# Revit family: Sanitary_Showers_hansgrohe_24581XXX-Raindance-Alive-Q-Showerpipe-210-340-1jet-EcoSmart-with-ShowerSelect-Comfort_NEW
name_source: partatom
category: Plumbing Fixtures
units: mm (PartAtom-declared; Revit-internal decimal feet)

## family parameters
Always vertical = No
Cut with Voids When Loaded = No
Maintain Annotation Orientation = No
OmniClass Number = 23.31.17.00
OmniClass Title = Showers
Part Type = Normal
Room Calculation Point = No
Round Connector Dimension = Use Diameter
Shared = No
Work Plane-Based = Yes

## types (1)
- Default - please load Revit Family Type Catalog
    Connector Description = Water Inlet 12.7mm
    Default Elevation = 1219 mm
    Description = Raindance Alive Q Showerpipe 210/340 1jet EcoSmart with ShowerSelect Comfort
    Diameter = 13 mm
    Manufacturer = Hansgrohe
    Material 1 = Hansgrohe - Metal - 000 Chrome
    Material 2 = Hansgrohe - Plastic - Graphite
    Model = 24581XXX
    Product Page URL = https://www.hansgrohe.com
    Product data url = https://bimobject.com
    URL = https://www.hansgrohe.com
    Version = 1

## geometry (parser evidence)
native form markers: Sweep x1
no freeform markers — native parametric forms only
